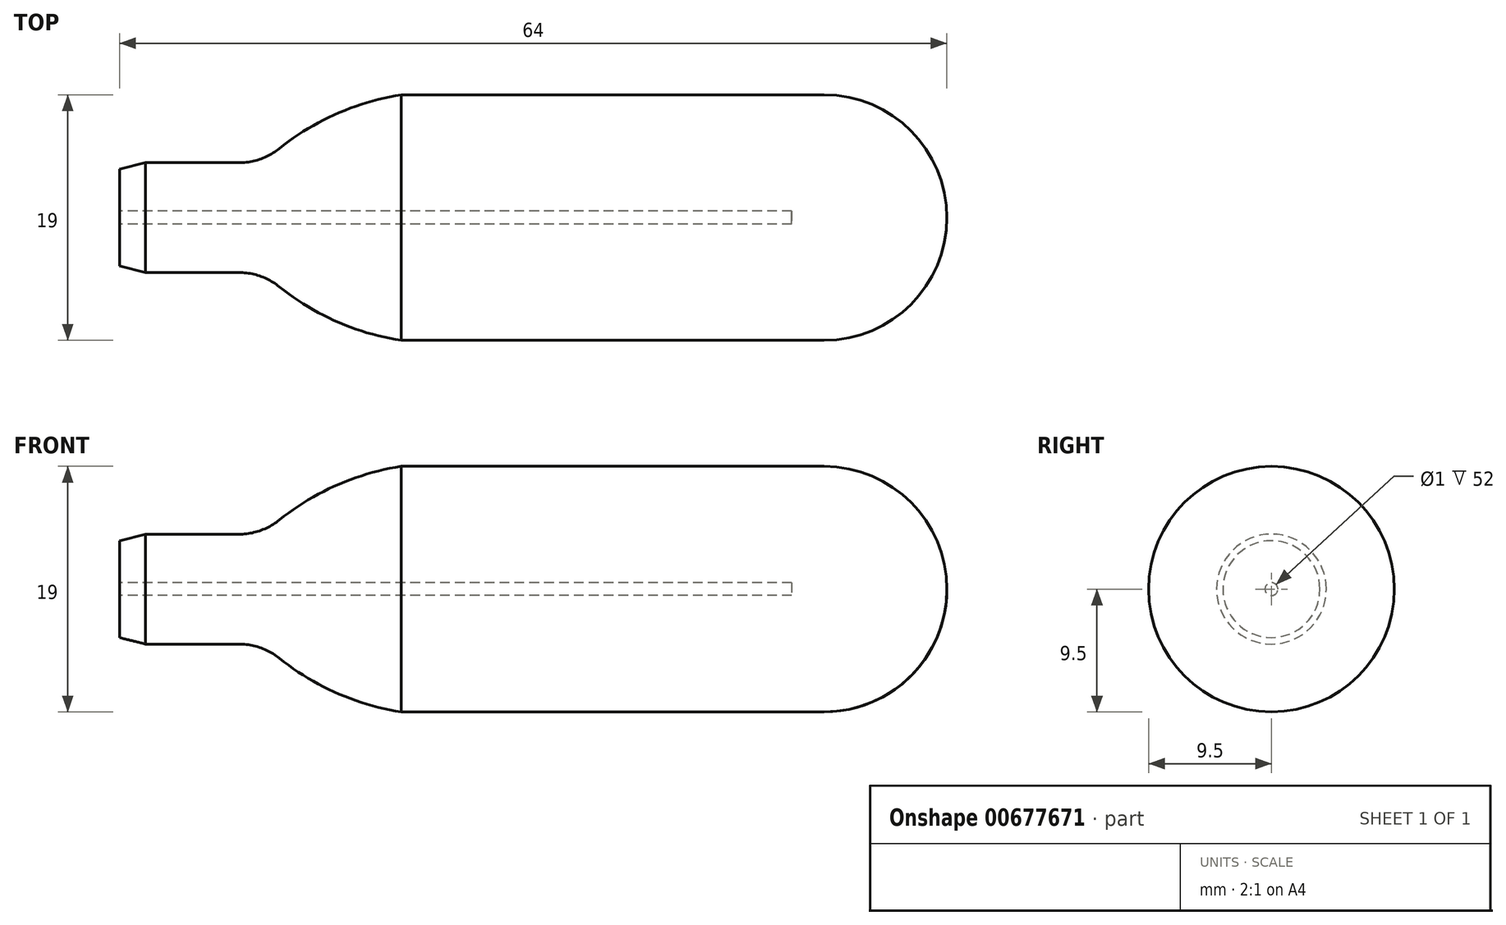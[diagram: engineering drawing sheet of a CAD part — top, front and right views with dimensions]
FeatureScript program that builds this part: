
annotation { "Feature Type Name" : "Feature", "Feature Type Description" : "" }
export const myFeature = defineFeature(function(context is Context, id is Id, definition is map)
    precondition{}
    {
        {
            var Q0;
            Q0=qCreatedBy(makeId("Front.planeOp"),FACE);
            var sketch = newSketch(context, id + "F0", { "sketchPlane" : qUnion([Q0])});
            skLineSegment(sketch, "E0", {"start": v(0, 0) * mm, "end": v(-64, 0) * mm});
            skLineSegment(sketch, "E1", {"start": v(0, 0) * mm, "end": v(-9.5, 0) * mm});
            skArc(sketch, "E2", {"start": v(0, 0) * mm, "mid": v(-2.78, 6.72) * mm, "end": v(-9.5, 9.5) * mm});
            skLineSegment(sketch, "E3.bottom", {"start": v(-64, 0) * mm, "end": v(-56, 0) * mm});
            skLineSegment(sketch, "E4", {"start": v(-42.21, 9.5) * mm, "end": v(-9.5, 9.5) * mm});
            skLineSegment(sketch, "E5", {"start": v(-62, 4.25) * mm, "end": v(-64, 3.75) * mm});
            skLineSegment(sketch, "E6", {"start": v(-62, 4.25) * mm, "end": v(-54.76, 4.25) * mm});
            skLineSegment(sketch, "E7", {"start": v(-64, 3.75) * mm, "end": v(-64, 0) * mm});
            skArc(sketch, "E8", {"start": v(-42.21, 9.5) * mm, "mid": v(-47.2, 8.04) * mm, "end": v(-51.64, 5.35) * mm});
            skPoint(sketch, "E9.visualSharp", {"position": v(-52.9, 4.25) * mm});
            skArc(sketch, "E9.filletArc", {"start": v(-54.76, 4.25) * mm, "mid": v(-53.1, 4.53) * mm, "end": v(-51.64, 5.35) * mm});
            skSolve(sketch);
        }
        {
            var Q0;
            Q0 = qSketchRegion(id + "F0", true);
            var Q1;
            Q1=sQuery(id+"F0.wireOp",EDGE,"E0");
            revolve(context, id + "F1", {"entities" : qUnion([Q0]), "axis" : qUnion([Q1]), "revolveType" : RevolveType.FULL});
        }
        {
            var Q0;
            Q0=makeQuery(id+"F1.opRevolve","SWEPT_FACE",FACE,{"disambiguationData":[OSD([sQuery(id+"F0.wireOp",EDGE,"E7")])]});
            var sketch = newSketch(context, id + "F2", { "sketchPlane" : qUnion([Q0])});
            skCircle(sketch, "E10", {"center": v(0, 0) * mm, "radius": 0.5 * mm});
            skSolve(sketch);
        }
        {
            var Q0;
            Q0=makeQuery(id+"F2.imprint","IMPRINT",FACE,{"disambiguationData":[TD([[makeQuery(id+"F2.imprint","IMPRINT",EDGE,{"derivedFrom":sQuery(id+"F2.wireOp",EDGE,"E10")}),1.0]])]});
            extrude(context, id + "F3", {"entities" : qUnion([Q0]), "operationType" : NewBodyOperationType.REMOVE, "oppositeDirection" : true, "depth" : 52 * mm, "offsetDistance" : 25 * mm});
        }
    });
